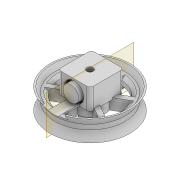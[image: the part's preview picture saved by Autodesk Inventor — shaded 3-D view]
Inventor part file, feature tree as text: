
AUTODESK INVENTOR PART (.ipt)
format: ipt  version: 2022 (Build 260153000, 153)  size: 478,208 bytes
history: native  units: mm
features: extrude x14, sketch x13, projected_geometry x11, chamfer x5, thicken_offset x2, plane x1, fillet x1
ambient origin geometry x8: Origin, YZ Plane, XZ Plane, XY Plane, X Axis, Y Axis, Z Axis, Center Point
bodies: Solid1 (feature_tree)
feature tree (47):
  extrude  "Extrusion1"  Depth=12.2mm
  extrude  "Extrusion2"  Depth=1.0mm
  extrude  "Extrusion3"  Depth=2.0mm TaperAngle=0.0deg
  plane  "Work Plane1"
  extrude  "Extrusion12"  Depth=10.0mm
  fillet  "Fillet5"  Radius=10.0mm
  extrude  "Extrusion14"  Depth=2.0mm
  extrude  "Extrusion15"  Depth=5.0mm TaperAngle=0.0deg
  extrude  "Extrusion16"  Depth=4.1mm
  extrude  "Extrusion17"  Depth=9.0mm
  sketch  "Sketch19"  dims[d79=3.0mm d80=2.0mm]
  extrude  "Extrusion18"  Depth=2.0mm
  extrude  "Extrusion19"  Depth=2.0mm
  thicken_offset  "Thicken1"
  extrude  "Extrusion20"  Depth=3.0mm TaperAngle=0.0deg
  extrude  "Extrusion21"  Depth=1.0mm
  chamfer  "Chamfer1"  Distance=2.0mm
  chamfer  "Chamfer2"  Distance=3.0mm
  chamfer  "Chamfer3"  Distance=2.0mm
  chamfer  "Chamfer4"  Distance=3.0mm
  sketch  "Sketch22"  dims[d86=4.1mm d87=2.0mm d88=3.0mm d89=2.0mm d90=3.0mm d91=2.4mm d92=0.0mm d94=17.0mm d95=2.0mm d96=0.0mm d97=1.5mm d98=2.0mm d99=0.0mm d100=100.0mm d101=0.0mm d102=12.0mm d103=12.0mm d104=3.0mm d105=3.0mm d106=0.0mm d107=3.0mm d108=8.0mm d109=8.0mm d110=3.0mm d111=0.0mm d112=3.0mm d113=5.0mm d114=45.0deg d115=3.0mm d116=5.0mm d117=45.0deg d118=2.0mm d119=3.0mm d120=45.0deg d121=2.0mm d122=3.0mm d123=45.0deg d124=37.0mm d125=19.0mm d126=1.5mm d127=1.5mm d128=30.0mm d130=360.0deg d132=6.0mm d133=0.0mm d134=8.0mm d135=0.0mm d136=2.0mm d137=2.0mm d138=45.0deg d139=2.0mm d140=2.0mm]
  extrude  "Extrusion22"  Depth=2.4mm TaperAngle=0.0deg
  extrude  "Extrusion23"  Depth=17.0mm
  chamfer  "Chamfer5"  Distance=2.0mm
  thicken_offset  "Thicken2"
  sketch  "Sketch1"  dims[d0=9.8mm d1=12.2mm]
  sketch  "Sketch2"  dims[d3=4.0mm d4=1.0mm]
  projected_geometry  "Projected Loop1"
  sketch  "Sketch3"  dims[d5=18.0mm d6=0.0mm d7=2.0mm d8=0.0mm]
  projected_geometry  "Projected Loop2"
  sketch  "Sketch6"  dims[d9=3.0mm d10=0.0mm d49=4.1mm d50=10.0mm]
  projected_geometry  "Projected Loop3"
  projected_geometry  "Projected Loop4"
  sketch  "Sketch14"  dims[d63=100.0mm d64=0.0mm d65=2.0mm]
  sketch  "Sketch15"  dims[d69=7.0mm d71=5.0mm d72=0.0mm]
  projected_geometry  "Projected Loop10"
  projected_geometry  "Projected Loop11"
  sketch  "Sketch16"  dims[d73=16.0mm d74=4.1mm]
  projected_geometry  "Projected Loop12"
  sketch  "Sketch17"  dims[d75=1.4mm d76=9.0mm]
  sketch  "Sketch18"  dims[d77=1.0mm d78=2.0mm]
  projected_geometry  "Projected Loop13"
  projected_geometry  "Projected Loop14"
  projected_geometry  "Projected Loop15"
  sketch  "Sketch20"  dims[d81=4.0mm d82=3.0mm d83=0.0mm]
  sketch  "Sketch21"  dims[d84=1.4mm d85=1.0mm]
  projected_geometry  "Projected Loop16"
